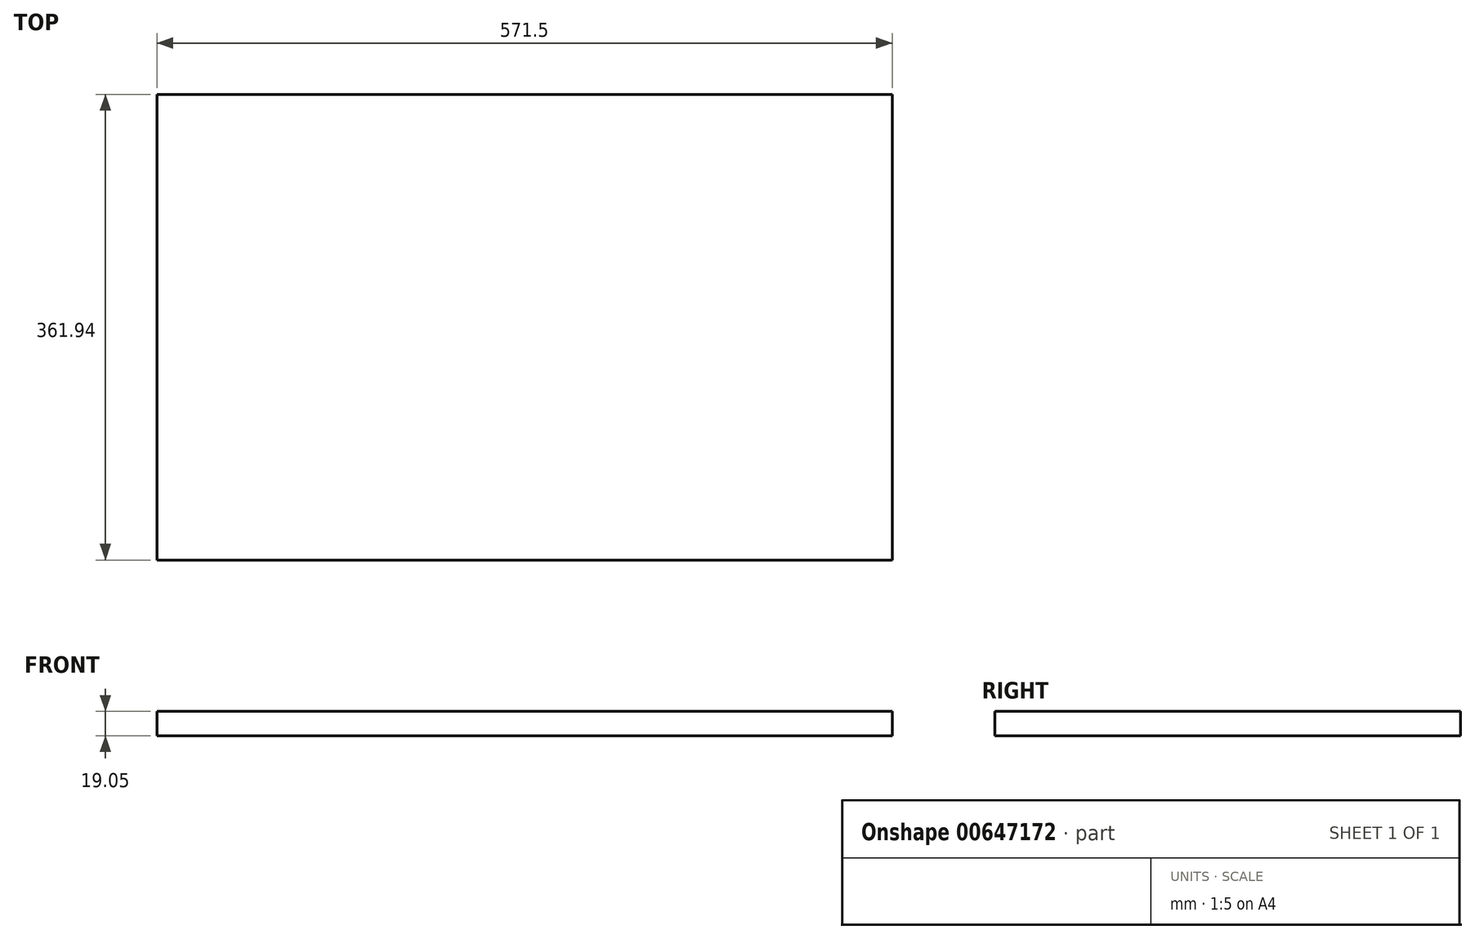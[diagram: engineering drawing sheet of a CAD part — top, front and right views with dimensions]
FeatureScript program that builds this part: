
annotation { "Feature Type Name" : "Feature", "Feature Type Description" : "" }
export const myFeature = defineFeature(function(context is Context, id is Id, definition is map)
    precondition{}
    {
        {
            var Q0;
            Q0=qCreatedBy(makeId("Top.planeOp"),FACE);
            var sketch = newSketch(context, id + "F0", { "sketchPlane" : qUnion([Q0])});
            skLineSegment(sketch, "E0.bottom", {"start": v(-285.75, 180.98) * mm, "end": v(285.75, 180.98) * mm});
            skLineSegment(sketch, "E0.top", {"start": v(-285.75, -180.98) * mm, "end": v(285.75, -180.98) * mm});
            skLineSegment(sketch, "E0.left", {"start": v(-285.75, 180.98) * mm, "end": v(-285.75, -180.98) * mm});
            skLineSegment(sketch, "E0.right", {"start": v(285.75, 180.98) * mm, "end": v(285.75, -180.98) * mm});
            skPoint(sketch, "E0.middle", {"position": v(0, 0) * mm});
            skSolve(sketch);
        }
        {
            var Q0;
            Q0=makeQuery(id+"F0.imprint","IMPRINT",FACE,{"disambiguationData":[TD([[makeQuery(id+"F0.imprint","IMPRINT",EDGE,{"derivedFrom":sQuery(id+"F0.wireOp",EDGE,"E0.bottom")}),-1.0]])]});
            extrude(context, id + "F1", {"entities" : qUnion([Q0]), "depth" : 19.05 * mm, "offsetDistance" : 25.4 * mm});
        }
    });
